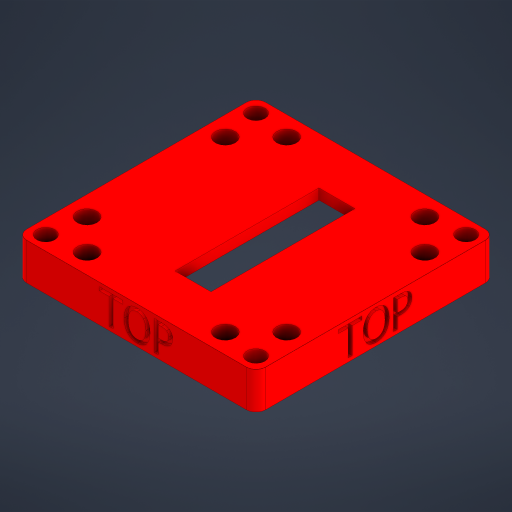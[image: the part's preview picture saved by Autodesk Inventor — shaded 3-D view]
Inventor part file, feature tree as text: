
AUTODESK INVENTOR PART (.ipt)
format: ipt  version: 2023.3 (Build 273359000, 359)  size: 550,400 bytes
history: native  units: mm
features: extrude x6, sketch x3, chamfer x2, projected_geometry x2, fillet x1, pattern_circular x1
ambient origin geometry x8: Origin, YZ Plane, XZ Plane, XY Plane, X Axis, Y Axis, Z Axis, Center Point
bodies: Solid1 (feature_tree)
feature tree (15):
  sketch  "Sketch1"  dims[d0=49.8mm d1=49.8mm]
  extrude  "Extrusion1"  Depth=49.8mm
  extrude  "Extrusion2"  Depth=3.0mm
  chamfer  "Chamfer1"  Distance=3.75mm
  fillet  "Fillet1"  Radius=4.2125mm
  chamfer  "Chamfer2"  Distance=0.675mm
  extrude  "Extrusion3"  Depth=30.0mm
  extrude  "Extrusion4"  Depth=30.0mm
  extrude  "Extrusion5"  Depth=30.0mm
  pattern_circular  "Circular Pattern1"  [2 undecoded]
  extrude  "Extrusion6"  Depth=30.0mm
  sketch  "Sketch2"  dims[d2=7.85mm d3=3.0mm]
  projected_geometry  "Projected Loop2"
  sketch  "Sketch3"  dims[d4=3.0mm d5=3.75mm d6=4.2125mm d7=0.675mm d8=10.5mm d9=10.5mm d10=4.1mm d11=4.14675mm d12=7.85mm d13=7.85mm d14=5.5mm d15=5.5mm d16=40.0mm d18=360.0deg d20=7.7mm d21=0.0mm d22=2.2mm d23=0.0mm d24=5.5mm d25=2.0mm d26=45.0deg d27=2.0mm d28=0.025mm d29=2.0mm d30=45.0deg d31=3.0mm d32=0.0mm d33=3.0mm d34=0.0mm d35=0.75mm d36=0.0mm d37=40.0mm d38=360.0deg d40=23.0mm d41=7.5mm d42=30.0mm d43=2.2mm d44=0.0mm]
  projected_geometry  "Projected Loop3"
note: 2 required parameter values undecoded (feature->parameter linkage not recoverable at this tier; creation-order binding heuristic only, values carry confidence <= 0.55)
